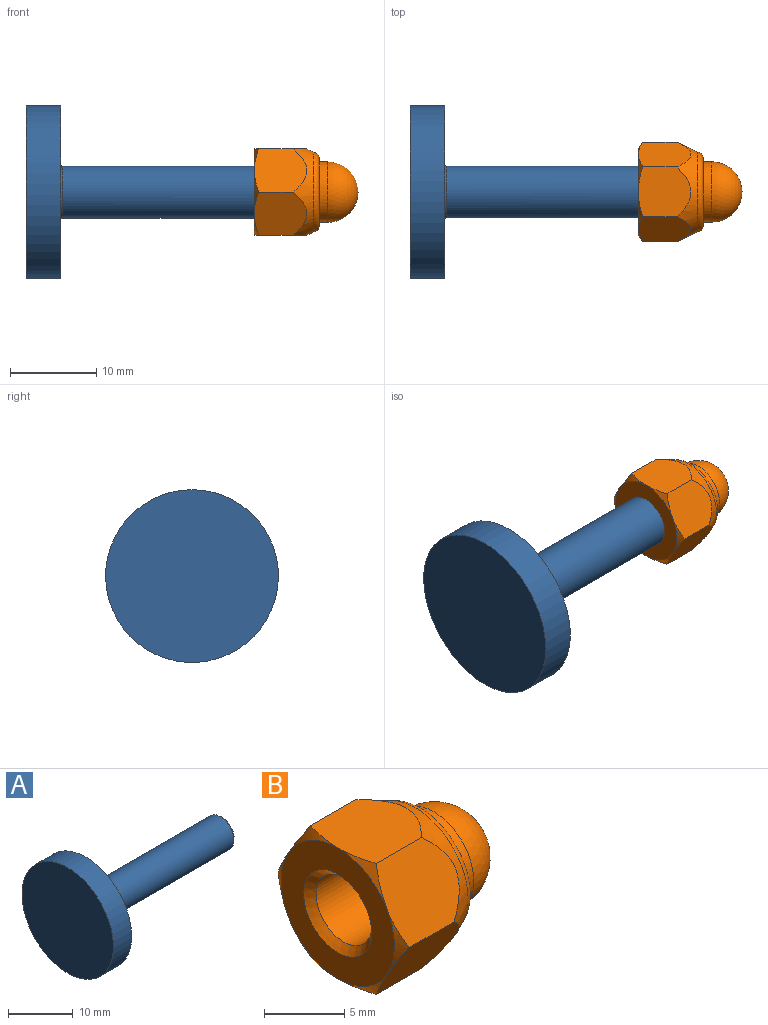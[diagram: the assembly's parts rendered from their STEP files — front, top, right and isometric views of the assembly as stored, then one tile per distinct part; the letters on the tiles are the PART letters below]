
ASSEMBLY  parts=2 mates=1
PART A: 7 faces, bbox 34x20x20 mm
  f0: plane 20x20mm, normal (1,0,0), area 281mm2, adj f1,f5
  f1: torus R=3.25mm, axis (1,0,0), area 7.6mm2, adj f0,f4
  f2: plane 4.77x4.77mm, normal (1,0,0), area 17.9mm2, adj f3
  f3: cone r=3mm half-angle=45deg, axis (-1,0,0), area 14.7mm2, adj f2,f4
  f4: cylinder r=3mm len=29.14mm, axis (1,0,0), area 549.2mm2, adj f1,f3
  f5: cylinder r=10mm len=20mm, axis (-1,0,0), area 251.3mm2, adj f0,f6
  f6: plane 20x20mm, normal (-1,0,0), area 314.2mm2, adj f5
PART B: 22 faces, bbox 12.5x12x12 mm
  f0: plane 10x10mm, normal (-1,0,0), area 50.3mm2, adj f1,f4,f5,f6,f7,f8,f9
  f1: cone r=3mm half-angle=45deg, axis (-1,0,0), area 13.1mm2, adj f0,f2
  f2: cylinder r=2.46mm len=6.42mm, axis (1,0,0), area 99.1mm2, adj f1,f3
  f3: cone r=2.46mm half-angle=45deg, axis (1,0,0), area 13.1mm2, adj f2,f21
  f4: cone r=5.77mm half-angle=56.8deg, axis (1,0,0), area 2.5mm2, adj f0,f11,f12
  f5: cone r=5.77mm half-angle=56.8deg, axis (1,0,0), area 2.5mm2, adj f0,f10,f11
  f6: cone r=5.77mm half-angle=56.8deg, axis (1,0,0), area 2.5mm2, adj f0,f10,f15
  f7: cone r=5.77mm half-angle=56.8deg, axis (1,0,0), area 2.5mm2, adj f0,f14,f15
  f8: cone r=5.77mm half-angle=56.8deg, axis (1,0,0), area 2.5mm2, adj f0,f13,f14
  f9: cone r=5.77mm half-angle=56.8deg, axis (1,0,0), area 2.5mm2, adj f0,f12,f13
  f10: plane 6.57x5.49mm, normal (0,-0.87,0.5), area 30.9mm2, adj f5,f6,f11,f15,f16
  f11: plane 6.57x5.49mm, normal (0,-0.87,-0.5), area 30.9mm2, adj f4,f5,f10,f12,f16
  f12: plane 6.57x6.27mm, normal (0,0,-1), area 30.9mm2, adj f4,f9,f11,f13,f16
  f13: plane 6.57x5.49mm, normal (0,0.87,-0.5), area 30.9mm2, adj f8,f9,f12,f14,f16
  f14: plane 6.57x5.49mm, normal (0,0.87,0.5), area 30.9mm2, adj f7,f8,f13,f15,f16
  f15: plane 6.57x6.27mm, normal (0,0,1), area 30.9mm2, adj f6,f7,f10,f14,f16
  f16: cone r=4.61mm half-angle=26deg, axis (-1,0,0), area 45.3mm2, adj f10,f11,f12,f13,f14,f15,f17
  f17: torus R=3.87mm, axis (1,0,0), area 28.4mm2, adj f16,f19
  f18: cylinder r=3.5mm len=7mm, axis (1,0,0), area 22mm2, adj f19,f20
  f19: plane 7.74x7.74mm, normal (1,0,0), area 8.5mm2, adj f17,f18
  f20: sphere r=3.5mm, area 77mm2, adj f18
  f21: cone r=3mm half-angle=51.3deg, axis (-1,0,0), area 36.2mm2, adj f3
PLACE A t=(-9.09,-0.02,-3.42)mm
PLACE B t=(13.34,-0.02,-3.42)mm
MATE revolute B.f1 <-> A.f3  axis (1,0,0) through (20.3,-0.02,-3.42)mm
